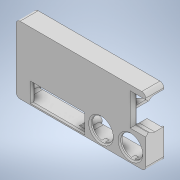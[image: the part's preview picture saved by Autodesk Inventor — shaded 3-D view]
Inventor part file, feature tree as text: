
AUTODESK INVENTOR PART (.ipt)
format: ipt  version: 2021 (Build 250183000, 183)  size: 609,280 bytes
history: native  units: mm
features: sketch x29, extrude x26, chamfer x9, fillet x8, hole x3
ambient origin geometry x8: Origin, YZ Plane, XZ Plane, XY Plane, X Axis, Y Axis, Z Axis, Center Point
bodies: Solid1 (feature_tree)
feature tree (75):
  extrude  "Extrusion1"  Depth=52.0mm
  extrude  "Extrusion2"  Depth=50.0mm
  extrude  "Extrusion3"  Depth=2.0mm
  extrude  "Extrusion4"  Depth=2.0mm
  fillet  "Fillet1"  Radius=2.0mm
  chamfer  "Chamfer1"  Distance=12.0mm
  extrude  "Extrusion5"  Depth=10.4mm
  extrude  "Extrusion6"  Depth=10.4mm
  extrude  "Extrusion7"  Depth=17.0mm
  extrude  "Extrusion8"  Depth=2.0mm
  extrude  "Extrusion9"  Depth=2.0mm
  chamfer  "Chamfer2"  Distance=2.0mm
  extrude  "Extrusion10"  Depth=2.0mm TaperAngle=45.0deg
  fillet  "Fillet3"  Radius=88.0mm
  chamfer  "Chamfer3"  Distance=20.0mm
  extrude  "Extrusion11"  Depth=2.0mm TaperAngle=0.0deg
  extrude  "Extrusion12"  Depth=11.0mm
  hole  "Hole1"  [1 undecoded]
  extrude  "Extrusion13"  TaperAngle=0.0deg  [1 undecoded]
  hole  "Hole2"  [1 undecoded]
  extrude  "Extrusion14"  Depth=2.0mm
  extrude  "Extrusion15"  Depth=2.0mm TaperAngle=45.0deg
  extrude  "Extrusion16"  Depth=40.0mm
  extrude  "Extrusion17"  Depth=6.0mm
  extrude  "Extrusion21"  Depth=2.0mm
  chamfer  "Chamfer6"  Distance=2.0mm
  extrude  "Extrusion22"  Depth=2.0mm TaperAngle=45.0deg
  extrude  "Extrusion23"  Depth=49.0mm
  extrude  "Extrusion24"  Depth=49.0mm
  chamfer  "Chamfer8"  Distance=2.0mm
  chamfer  "Chamfer9"  Distance=2.0mm
  fillet  "Fillet5"  Radius=5.0mm
  extrude  "Extrusion25"  Depth=2.0mm
  fillet  "Fillet6"  Radius=5.0mm
  chamfer  "Chamfer11"  Distance=12.0mm
  extrude  "Extrusion26"  Depth=2.0mm
  hole  "Hole3"  [1 undecoded]
  chamfer  "Chamfer12"  Distance=2.0mm
  fillet  "Fillet7"  Radius=5.0mm
  extrude  "Extrusion29"  Depth=2.0mm TaperAngle=0.0deg
  chamfer  "Chamfer13"  Distance=8.0mm
  extrude  "Extrusion30"  Depth=2.0mm
  extrude  "Extrusion31"  Depth=2.0mm
  fillet  "Fillet10"  Radius=12.0mm
  fillet  "Fillet11"  Radius=7.0mm
  fillet  "Fillet12"  Radius=5.8mm
  sketch  "Sketch1"  dims[d0=100.0mm d1=52.0mm]
  sketch  "Sketch2"  dims[d2=26.0mm d3=50.0mm]
  sketch  "Sketch3"  dims[d4=2.0mm d5=0.0mm d6=2.0mm]
  sketch  "Sketch4"  dims[d7=2.0mm d8=2.0mm d9=2.0mm d10=12.0mm d11=0.0mm]
  sketch  "Sketch5"  dims[d12=65.5mm d13=10.4mm]
  sketch  "Sketch6"  dims[d14=88.25mm d15=10.4mm]
  sketch  "Sketch7"  dims[d16=17.0mm d17=17.0mm]
  sketch  "Sketch8"  dims[d18=2.0mm d19=0.0mm d20=40.0mm]
  sketch  "Sketch9"  dims[d21=13.0mm d22=2.0mm]
  sketch  "Sketch10"  dims[d23=12.0mm d24=2.0mm d25=0.0mm]
  sketch  "Sketch11"  dims[d26=3.0mm d27=1.0mm d28=2.0mm d29=45.0deg d30=88.0mm]
  sketch  "Sketch12"  dims[d31=29.0mm]
  sketch  "Sketch13"  dims[d32=23.0mm d33=20.0mm d34=0.0mm]
  sketch  "Sketch14"  dims[d35=2.0mm d36=0.0mm d37=2.0mm d38=0.0mm]
  sketch  "Sketch15"  dims[d39=11.0mm d40=11.0mm]
  sketch  "Sketch16"  dims[d41=42.0mm d42=29.0mm]
  sketch  "Sketch17"  dims[d43=7.0mm d44=0.0mm]
  sketch  "Sketch18"  dims[d45=5.8mm d46=5.8mm]
  sketch  "Sketch19"  dims[d47=2.0mm d48=0.0mm d49=12.0mm]
  sketch  "Sketch23"  dims[d50=20.0mm d51=0.0mm d52=2.0mm d53=2.0mm d54=45.0deg]
  sketch  "Sketch24"  dims[d56=30.0mm d57=40.0mm]
  sketch  "Sketch25"  dims[d58=3.5mm d59=6.0mm]
  sketch  "Sketch27"  dims[d60=14.0mm d61=16.0mm d62=2.0mm d63=0.0mm]
  sketch  "Sketch28"  dims[d64=1.0mm d65=1.0mm d66=2.0mm d67=45.0deg]
  sketch  "Sketch29"  dims[d68=3.0mm d69=49.0mm]
  sketch  "Sketch30"  dims[d70=60.0mm d71=49.0mm]
  sketch  "Sketch33"  dims[d72=85.0mm]
  sketch  "Sketch34"  dims[d73=49.0mm]
  sketch  "Sketch35"  dims[d74=2.0mm d75=2.0mm d76=2.0mm d77=5.0mm d78=5.0mm d79=5.0mm d80=12.0mm d81=0.0mm d82=3.0mm d83=3.0mm d84=2.0mm d85=5.0mm d86=12.0mm d87=0.0mm d88=2.0mm d89=6.0mm d90=4.0mm d91=2.0mm d92=90.0deg d93=6.5mm d94=20.594885mm d95=8.0mm d96=97.0mm d97=4.2mm d98=12.0mm d99=0.0mm d100=2.0mm d101=6.0mm d102=4.0mm d103=2.0mm d104=90.0deg d105=6.5mm d106=20.594885mm d107=7.0mm d108=5.8mm d109=5.8mm d110=2.0mm d111=11.0mm d112=0.0mm d113=1.0mm d114=0.0mm d115=2.0mm d116=10.0mm d117=0.0mm d118=0.0mm d119=1.0mm d120=0.0mm d161=5.0mm d162=1.0mm d163=1.0mm d164=11.0mm d165=0.0mm d166=4.0mm d167=2.0mm d168=45.0deg d169=7.0mm d170=14.0mm d171=0.0mm d172=12.0mm d173=10.0mm d174=0.0mm d182=4.0mm d183=0.0mm d184=0.0mm d185=10.0mm d186=0.0mm d187=2.0mm d188=2.0mm d189=45.0deg d190=2.0mm d191=2.0mm d192=45.0deg d193=3.0mm d194=17.0mm d195=17.0mm d196=5.0mm d197=0.0mm d201=2.0mm d202=1.5mm d203=2.0mm d204=45.0deg d205=50.0mm d206=3.0mm d207=5.0mm d208=7.5mm d209=0.0mm d210=2.0mm d211=6.0mm d212=4.0mm d213=2.0mm d214=90.0deg d215=6.5mm d216=20.594885mm d217=3.49mm d218=2.0mm d219=45.0deg d220=2.0mm d236=2.0mm d237=0.0mm d238=2.0mm d239=2.0mm d240=45.0deg d241=0.5mm d242=0.0mm d243=1.5mm d244=14.0mm d245=0.0mm d246=2.0mm d247=2.0mm d248=2.0mm d160=0.5mm d221=0.375mm]
note: 4 required parameter values undecoded (feature->parameter linkage not recoverable at this tier; creation-order binding heuristic only, values carry confidence <= 0.55)
